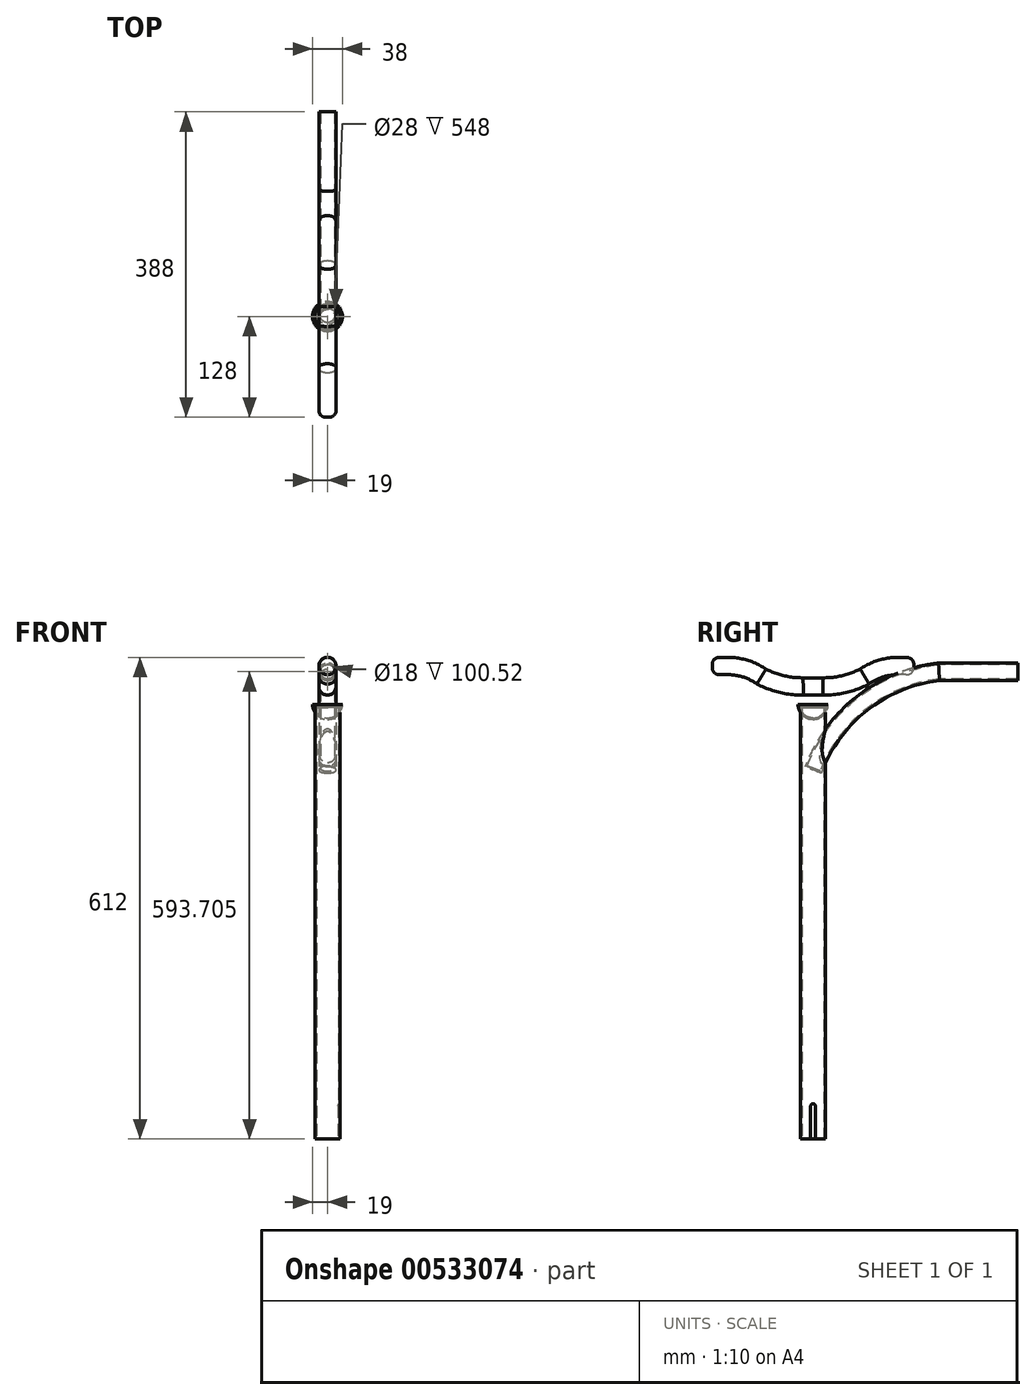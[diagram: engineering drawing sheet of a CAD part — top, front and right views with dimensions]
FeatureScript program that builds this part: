
annotation { "Feature Type Name" : "Feature", "Feature Type Description" : "" }
export const myFeature = defineFeature(function(context is Context, id is Id, definition is map)
    precondition{}
    {
        {
            var Q0;
            Q0=qCreatedBy(makeId("Top.planeOp"),FACE);
            var sketch = newSketch(context, id + "F0", { "sketchPlane" : qUnion([Q0])});
            skCircle(sketch, "E0", {"center": v(0, 0) * mm, "radius": 16 * mm});
            skSolve(sketch);
        }
        {
            var Q0;
            Q0 = qSketchRegion(id + "F0", true);
            extrude(context, id + "F1", {"entities" : qUnion([Q0]), "depth" : 550 * mm, "offsetDistance" : 25 * mm});
        }
        {
            var Q0;
            Q0=makeQuery(id+"F1.opExtrude","CAP_FACE",FACE,{"disambiguationData":[OSD([sQuery(id+"F0.wireOp",EDGE,"E0")])],"isStart":true});
            shell(context, id + "F2", {"entities" : qUnion([Q0]), "thickness" : 2 * mm});
        }
        {
            var Q0;
            Q0=qCreatedBy(makeId("Right.planeOp"),FACE);
            var sketch = newSketch(context, id + "F3", { "sketchPlane" : qUnion([Q0])});
            skLineSegment(sketch, "E1.bottom", {"start": v(3, 0) * mm, "end": v(-3, 0) * mm});
            skLineSegment(sketch, "E1.top", {"start": v(0, 45) * mm, "end": v(0, 45) * mm});
            skLineSegment(sketch, "E1.left", {"start": v(3, 0) * mm, "end": v(3, 42) * mm});
            skLineSegment(sketch, "E1.right", {"start": v(-3, 0) * mm, "end": v(-3, 42) * mm});
            skPoint(sketch, "E2.visualSharp", {"position": v(3, 45) * mm});
            skArc(sketch, "E2.filletArc", {"start": v(3, 42) * mm, "mid": v(2.12, 44.12) * mm, "end": v(0, 45) * mm});
            skPoint(sketch, "E3.visualSharp", {"position": v(-3, 45) * mm});
            skArc(sketch, "E3.filletArc", {"start": v(0, 45) * mm, "mid": v(-2.12, 44.12) * mm, "end": v(-3, 42) * mm});
            skSolve(sketch);
        }
        {
            var Q0;
            Q0 = qSketchRegion(id + "F3", true);
            extrude(context, id + "F4", {"entities" : qUnion([Q0]), "operationType" : NewBodyOperationType.REMOVE, "endBound" : BoundingType.THROUGH_ALL, "depth" : 25 * mm, "offsetDistance" : 25 * mm});
        }
        {
            var Q0;
            Q0=qCreatedBy(makeId("Right.planeOp"),FACE);
            var sketch = newSketch(context, id + "F5", { "sketchPlane" : qUnion([Q0])});
            skArc(sketch, "E4", {"start": v(160, 593.7) * mm, "mid": v(62.48, 553.73) * mm, "end": v(0, 468.85) * mm});
            skLineSegment(sketch, "E5", {"start": v(160, 593.7) * mm, "end": v(260, 593.7) * mm});
            skSolve(sketch);
        }
        {
            var Q0;
            Q0=sQuery(id+"F5.wireOp",VERTEX,"E5.end");
            var Q1;
            Q1=qCreatedBy(makeId("Front.planeOp"),FACE);
            cPlane(context, id + "F6", {"entities" : qUnion([Q0, Q1]), "cplaneType" : CPlaneType.PLANE_POINT, "offset" : 25 * mm, "width" : 150 * mm, "height" : 150 * mm});
        }
        {
            var Q0;
            Q0=qCreatedBy(id+"F6.planeOp",FACE);
            var sketch = newSketch(context, id + "F7", { "sketchPlane" : qUnion([Q0])});
            skCircle(sketch, "E6", {"center": v(0, 593.7) * mm, "radius": 11 * mm});
            skSolve(sketch);
        }
        {
            var Q0;
            Q0 = qSketchRegion(id + "F7", true);
            var Q1;
            Q1 = qConstructionFilter(qBodyType(qCreatedBy(id + "F5" ,EDGE), BodyType.WIRE), ConstructionObject.NO);
            sweep(context, id + "F8", {"operationType" : NewBodyOperationType.ADD, "profiles" : qUnion([Q0]), "path" : qUnion([Q1])});
        }
        {
            var Q0;
            Q0=makeQuery(id+"F8.opSweep","CAP_FACE",FACE,{"disambiguationData":[OSD([sQuery(id+"F5.wireOp",VERTEX,"E5.end"),sQuery(id+"F7.wireOp",EDGE,"E6")])],"isStart":true});
            shell(context, id + "F9", {"entities" : qUnion([Q0]), "thickness" : 2 * mm});
        }
        {
            var Q0;
            Q0=qCreatedBy(makeId("Right.planeOp"),FACE);
            var sketch = newSketch(context, id + "F10", { "sketchPlane" : qUnion([Q0])});
            skLineSegment(sketch, "E7", {"start": v(-128, 601) * mm, "end": v(-108, 601) * mm});
            skArc(sketch, "E8", {"start": v(-65.55, 587.62) * mm, "mid": v(-85.75, 597.58) * mm, "end": v(-108, 601) * mm});
            skArc(sketch, "E9", {"start": v(-65.55, 587.62) * mm, "mid": v(-39.8, 578.03) * mm, "end": v(-12.5, 575) * mm});
            skLineSegment(sketch, "E10", {"start": v(-12.5, 575) * mm, "end": v(0, 575) * mm});
            skLineSegment(sketch, "E11", {"start": v(0, 0) * mm, "end": v(0, 575) * mm, "construction": true});
            skArc(sketch, "E12.MirrorCS", {"start": v(65.55, 587.62) * mm, "mid": v(85.75, 597.58) * mm, "end": v(108, 601) * mm});
            skArc(sketch, "E13.MirrorCS", {"start": v(65.55, 587.62) * mm, "mid": v(39.8, 578.03) * mm, "end": v(12.5, 575) * mm});
            skLineSegment(sketch, "E14.MirrorCS", {"start": v(128, 601) * mm, "end": v(108, 601) * mm});
            skLineSegment(sketch, "E15", {"start": v(12.5, 575) * mm, "end": v(0, 575) * mm});
            skSolve(sketch);
        }
        {
            var Q0;
            Q0=sQuery(id+"F10.wireOp",VERTEX,"E14.MirrorCS.start");
            var Q1;
            Q1=qCreatedBy(id+"F6.planeOp",FACE);
            cPlane(context, id + "F11", {"entities" : qUnion([Q0, Q1]), "cplaneType" : CPlaneType.PLANE_POINT, "offset" : 25 * mm, "width" : 150 * mm, "height" : 150 * mm});
        }
        {
            var Q0;
            Q0=qCreatedBy(id+"F11.planeOp",FACE);
            var sketch = newSketch(context, id + "F12", { "sketchPlane" : qUnion([Q0])});
            skCircle(sketch, "E16", {"center": v(0, 601) * mm, "radius": 11 * mm});
            skSolve(sketch);
        }
        {
            var Q0;
            Q0 = qSketchRegion(id + "F12", true);
            var Q1;
            Q1 = qConstructionFilter(qBodyType(qCreatedBy(id + "F10" ,EDGE), BodyType.WIRE), ConstructionObject.NO);
            sweep(context, id + "F13", {"profiles" : qUnion([Q0]), "path" : qUnion([Q1])});
        }
        {
            var Q0;
            Q0=makeQuery(id+"F13.opSweep","CAP_EDGE",EDGE,{"disambiguationData":[OSD([sQuery(id+"F10.wireOp",VERTEX,"E7.start"),sQuery(id+"F12.wireOp",EDGE,"E16")])],"isStart":false});
            var Q1;
            {var subQ0=sQuery(id+"F12.wireOp",EDGE,"E16");var subQ1=sQuery(id+"F10.wireOp",VERTEX,"E14.MirrorCS.start");Q1=makeQuery(id+"F13.boolean.opBoolean","SPLIT",EDGE,{"disambiguationData":[TD([makeQuery(id+"F8.opSweep","SWEPT_FACE",FACE,{"disambiguationData":[OSD([sQuery(id+"F5.wireOp",EDGE,"E4"),sQuery(id+"F7.wireOp",EDGE,"E6")])]})])],"derivedFrom":makeQuery(id+"F13.opSweep","CAP_EDGE",EDGE,{"disambiguationData":[OSD([subQ1,subQ0])],"isStart":true})});}
            fillet(context, id + "F14", {"entities" : qUnion([Q0, Q1]), "radius" : 10 * mm, "tangentPropagation" : true, "rho" : 0.5, "crossSection" : FilletCrossSection.CONIC, "allowEdgeOverflow" : false});
        }
        {
            var Q0;
            Q0=qCreatedBy(makeId("Right.planeOp"),FACE);
            var sketch = newSketch(context, id + "F15", { "sketchPlane" : qUnion([Q0])});
            skArc(sketch, "E17", {"start": v(-19, 552) * mm, "mid": v(-13.44, 538.56) * mm, "end": v(0, 533) * mm});
            skLineSegment(sketch, "E18", {"start": v(0, 552) * mm, "end": v(0, 533) * mm});
            skLineSegment(sketch, "E19", {"start": v(0, 552) * mm, "end": v(-19, 552) * mm});
            skSolve(sketch);
        }
        {
            var Q0;
            Q0 = qSketchRegion(id + "F15", true);
            var Q1;
            Q1=sQuery(id+"F15.wireOp",EDGE,"E18");
            revolve(context, id + "F16", {"surfaceOperationType" : NewSurfaceOperationType.NEW, "entities" : qUnion([Q0]), "axis" : qUnion([Q1]), "revolveType" : RevolveType.FULL});
        }
        {
            var Q0;
            Q0=makeQuery(id+"F16.opRevolve","SWEPT_FACE",FACE,{"disambiguationData":[OSD([sQuery(id+"F15.wireOp",EDGE,"E19")])]});
            shell(context, id + "F17", {"entities" : qUnion([Q0]), "thickness" : 2 * mm});
        }
    });
